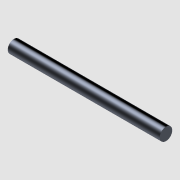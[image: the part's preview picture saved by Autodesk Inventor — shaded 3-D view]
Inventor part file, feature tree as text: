
AUTODESK INVENTOR PART (.ipt)
format: ipt  version: 2021 (Build 250183000, 183)  size: 103,936 bytes
history: native  units: in
note: dims shown in document units (in); Inventor stores cm internally (conversion verified against a paired STEP export)
features: extrude x2, other x1, imported_body x1, sketch x1
ambient origin geometry x8: Origin, YZ Plane, XZ Plane, XY Plane, X Axis, Y Axis, Z Axis, Center Point
bodies: Body1 (feature_tree)
feature tree (5):
  other  "Pin"
  extrude  "Extrude1"  TaperAngle=0.0deg  [1 undecoded]
  extrude  "Extrusion1"  [1 undecoded]
  imported_body  "Base1"
  sketch  "Sketch1"  dims[d1=1.0in d2=0.0in]
note: 2 required parameter values undecoded (feature->parameter linkage not recoverable at this tier; creation-order binding heuristic only, values carry confidence <= 0.55)
